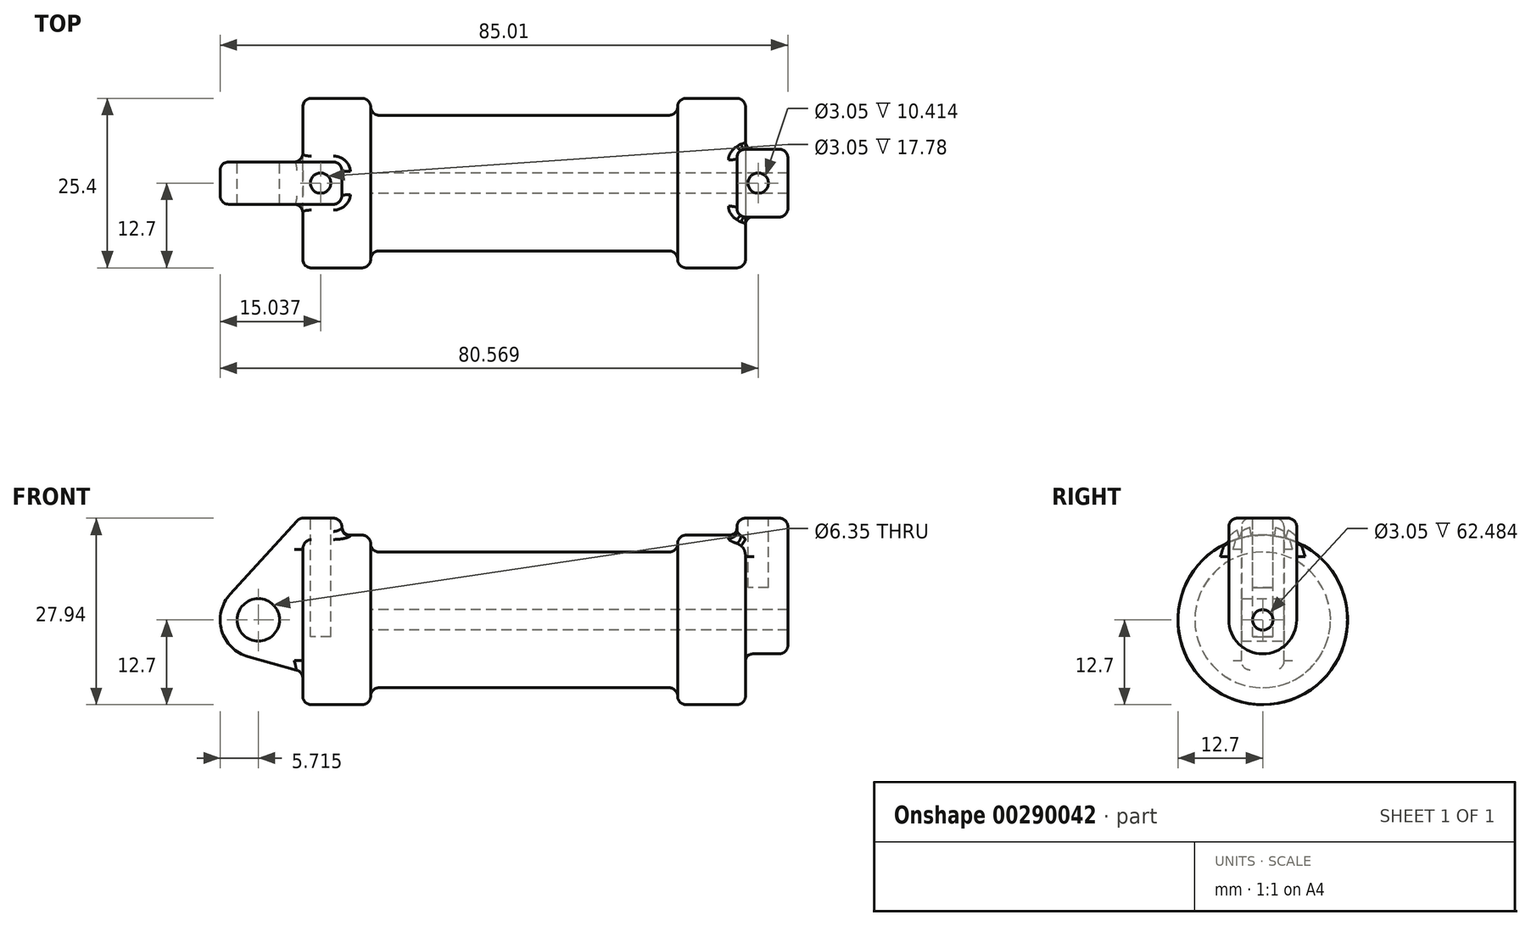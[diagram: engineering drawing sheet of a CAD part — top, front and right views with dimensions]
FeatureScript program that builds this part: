
annotation { "Feature Type Name" : "Feature", "Feature Type Description" : "" }
export const myFeature = defineFeature(function(context is Context, id is Id, definition is map)
    precondition{}
    {
        {
            var Q0;
            Q0=qCreatedBy(makeId("Front.planeOp"),FACE);
            var sketch = newSketch(context, id + "F0", { "sketchPlane" : qUnion([Q0])});
            skLineSegment(sketch, "E0", {"start": v(0, 0) * mm, "end": v(0, 12.7) * mm});
            skLineSegment(sketch, "E1", {"start": v(0, 12.7) * mm, "end": v(10.16, 12.7) * mm});
            skLineSegment(sketch, "E2", {"start": v(10.16, 12.7) * mm, "end": v(10.16, 10.16) * mm});
            skLineSegment(sketch, "E3", {"start": v(10.16, 10.16) * mm, "end": v(56.13, 10.16) * mm});
            skLineSegment(sketch, "E4", {"start": v(56.13, 10.16) * mm, "end": v(56.13, 12.7) * mm});
            skLineSegment(sketch, "E5", {"start": v(56.13, 12.7) * mm, "end": v(66.3, 12.7) * mm});
            skLineSegment(sketch, "E6", {"start": v(66.3, 12.7) * mm, "end": v(66.3, 0) * mm});
            skLineSegment(sketch, "E7", {"start": v(66.3, 0) * mm, "end": v(0, 0) * mm});
            skLineSegment(sketch, "E8", {"start": v(5.84, 15.24) * mm, "end": v(-0.5, 15.24) * mm});
            skLineSegment(sketch, "E9", {"start": v(-0.5, 15.24) * mm, "end": v(-10.88, 3.85) * mm});
            skLineSegment(sketch, "E10", {"start": v(0, 0) * mm, "end": v(-6.65, 0) * mm});
            skCircle(sketch, "E11", {"center": v(-6.65, 0) * mm, "radius": 5.72 * mm});
            skCircle(sketch, "E12", {"center": v(-6.65, 0) * mm, "radius": 3.18 * mm});
            skLineSegment(sketch, "E13", {"start": v(5.84, 15.24) * mm, "end": v(5.84, -9.4) * mm});
            skLineSegment(sketch, "E14", {"start": v(5.84, -9.4) * mm, "end": v(-8.18, -5.5) * mm});
            skSolve(sketch);
        }
        {
            var Q0;
            {var subQ0=sQuery(id+"F0.wireOp",EDGE,"E14");Q0=makeQuery(id+"F0.imprint","IMPRINT",FACE,{"disambiguationData":[TD([[makeQuery(id+"F0.imprint","IMPRINT",EDGE,{"derivedFrom":subQ0}),-1.0]])]});}
            var Q1;
            {var subQ5=sQuery(id+"F0.wireOp",EDGE,"E12");Q1=makeQuery(id+"F0.imprint","IMPRINT",FACE,{"disambiguationData":[TD([[makeQuery(id+"F0.imprint","IMPRINT",EDGE,{"derivedFrom":subQ5}),-1.0]])]});}
            var Q2;
            {var subQ1=sQuery(id+"F0.wireOp",EDGE,"E0");Q2=makeQuery(id+"F0.imprint","IMPRINT",FACE,{"disambiguationData":[TD([[makeQuery(id+"F0.imprint","IMPRINT",EDGE,{"derivedFrom":subQ1}),1.0]])]});}
            var Q3;
            {var subQ0=sQuery(id+"F0.wireOp",EDGE,"E0");Q3=makeQuery(id+"F0.imprint","IMPRINT",FACE,{"disambiguationData":[TD([[makeQuery(id+"F0.imprint","IMPRINT",EDGE,{"derivedFrom":subQ0}),-1.0]])]});}
            extrude(context, id + "F1", {"entities" : qUnion([Q0, Q1, Q2, Q3]), "endBound" : BoundingType.SYMMETRIC, "depth" : 6.35 * mm});
        }
        {
            var Q0;
            {var subQ0=sQuery(id+"F0.wireOp",EDGE,"E0");Q0=makeQuery(id+"F0.imprint","IMPRINT",FACE,{"disambiguationData":[TD([[makeQuery(id+"F0.imprint","IMPRINT",EDGE,{"derivedFrom":subQ0}),-1.0]])]});}
            var Q1;
            {var subQ0=sQuery(id+"F0.wireOp",EDGE,"E2");Q1=makeQuery(id+"F0.imprint","IMPRINT",FACE,{"disambiguationData":[TD([[makeQuery(id+"F0.imprint","IMPRINT",EDGE,{"derivedFrom":subQ0}),-1.0]])]});}
            var Q2;
            Q2=sQuery(id+"F0.wireOp",EDGE,"E7");
            revolve(context, id + "F2", {"operationType" : NewBodyOperationType.ADD, "entities" : qUnion([Q0, Q1]), "axis" : qUnion([Q2]), "revolveType" : RevolveType.FULL});
        }
        {
            var Q0;
            Q0=makeQuery(id+"F2.opRevolve","SWEPT_FACE",FACE,{"disambiguationData":[OSD([sQuery(id+"F0.wireOp",EDGE,"E6")])]});
            var sketch = newSketch(context, id + "F3", { "sketchPlane" : qUnion([Q0])});
            skCircle(sketch, "E15", {"center": v(0, 0) * mm, "radius": 5.08 * mm});
            skCircle(sketch, "E16", {"center": v(0, 0) * mm, "radius": 1.52 * mm});
            skLineSegment(sketch, "E17", {"start": v(-5.08, 0) * mm, "end": v(-5.08, 15.24) * mm});
            skLineSegment(sketch, "E18", {"start": v(-5.08, 15.24) * mm, "end": v(5.08, 15.24) * mm});
            skLineSegment(sketch, "E19", {"start": v(5.08, 15.24) * mm, "end": v(5.08, 0) * mm});
            skSolve(sketch);
        }
        {
            var Q0;
            Q0 = qSketchRegion(id + "F3", true);
            extrude(context, id + "F4", {"entities" : qUnion([Q0]), "operationType" : NewBodyOperationType.ADD, "depth" : 6.35 * mm, "hasSecondDirection" : true, "secondDirectionOppositeDirection" : true, "secondDirectionDepth" : 1.27 * mm});
        }
        {
            var Q0;
            Q0=makeQuery(id+"F3.imprint","IMPRINT",FACE,{"disambiguationData":[TD([[makeQuery(id+"F3.imprint","IMPRINT",EDGE,{"derivedFrom":sQuery(id+"F3.wireOp",EDGE,"E16")}),1.0]])]});
            var Q1;
            Q1=makeQuery(id+"F2.opRevolve","SWEPT_FACE",FACE,{"disambiguationData":[OSD([sQuery(id+"F0.wireOp",EDGE,"E2")])]});
            extrude(context, id + "F5", {"entities" : qUnion([Q0]), "operationType" : NewBodyOperationType.REMOVE, "endBound" : BoundingType.UP_TO_SURFACE, "oppositeDirection" : true, "endBoundEntityFace" : qUnion([Q1]), "depth" : 25.4 * mm});
        }
        {
            var Q0;
            {var subQ0=sQuery(id+"F3.wireOp",EDGE,"E18");Q0=makeQuery(id+"FFKBswe1jkoV0Kr_1.boolean.opBoolean","MERGE",FACE,{"derivedFrom":[makeQuery(id+"F4.opExtrude","SWEPT_FACE",FACE,{"disambiguationData":[OSD([subQ0])]}),makeQuery(id+"FFKBswe1jkoV0Kr_1.opExtrude","SWEPT_FACE",FACE,{"disambiguationData":[OSD([subQ0])]})]});}
            var sketch = newSketch(context, id + "F6", { "sketchPlane" : qUnion([Q0])});
            skCircle(sketch, "E20", {"center": v(68.2, 0) * mm, "radius": 1.52 * mm});
            skSolve(sketch);
        }
        {
            var Q0;
            Q0=makeQuery(id+"F6.imprint","IMPRINT",FACE,{"disambiguationData":[TD([[makeQuery(id+"F6.imprint","IMPRINT",EDGE,{"derivedFrom":sQuery(id+"F6.wireOp",EDGE,"E20")}),1.0]])]});
            extrude(context, id + "F7", {"entities" : qUnion([Q0]), "operationType" : NewBodyOperationType.REMOVE, "oppositeDirection" : true, "depth" : 10.4 * mm});
        }
        {
            var Q0;
            Q0=makeQuery(id+"F1.opExtrude","SWEPT_FACE",FACE,{"disambiguationData":[OSD([sQuery(id+"F0.wireOp",EDGE,"E8")])]});
            var sketch = newSketch(context, id + "F8", { "sketchPlane" : qUnion([Q0])});
            skCircle(sketch, "E21", {"center": v(2.67, 0) * mm, "radius": 1.52 * mm});
            skSolve(sketch);
        }
        {
            var Q0;
            Q0=makeQuery(id+"F8.imprint","IMPRINT",FACE,{"disambiguationData":[TD([[makeQuery(id+"F8.imprint","IMPRINT",EDGE,{"derivedFrom":sQuery(id+"F8.wireOp",EDGE,"E21")}),1.0]])]});
            extrude(context, id + "F9", {"entities" : qUnion([Q0]), "operationType" : NewBodyOperationType.REMOVE, "oppositeDirection" : true, "depth" : 17.78 * mm});
        }
        {
            var Q0;
            Q0=makeQuery(id+"F1.opExtrude","CAP_EDGE",EDGE,{"disambiguationData":[OSD([sQuery(id+"F0.wireOp",EDGE,"E9")])],"isStart":false});
            var Q1;
            Q1=makeQuery(id+"F1.opExtrude","CAP_EDGE",EDGE,{"disambiguationData":[OSD([sQuery(id+"F0.wireOp",EDGE,"E11")])],"isStart":false});
            var Q2;
            Q2=makeQuery(id+"F1.opExtrude","CAP_EDGE",EDGE,{"disambiguationData":[OSD([sQuery(id+"F0.wireOp",EDGE,"E11")])],"isStart":true});
            var Q3;
            Q3=makeQuery(id+"F1.opExtrude","CAP_EDGE",EDGE,{"disambiguationData":[OSD([sQuery(id+"F0.wireOp",EDGE,"E9")])],"isStart":true});
            var Q4;
            Q4=makeQuery(id+"F1.opExtrude","CAP_EDGE",EDGE,{"disambiguationData":[OSD([sQuery(id+"F0.wireOp",EDGE,"E14")])],"isStart":true});
            var Q5;
            Q5=makeQuery(id+"F1.opExtrude","CAP_EDGE",EDGE,{"disambiguationData":[OSD([sQuery(id+"F0.wireOp",EDGE,"E14")])],"isStart":false});
            var Q6;
            Q6=makeQuery(id+"F1.opExtrude","CAP_EDGE",EDGE,{"disambiguationData":[OSD([sQuery(id+"F0.wireOp",EDGE,"E8")])],"isStart":true});
            var Q7;
            Q7=makeQuery(id+"F1.opExtrude","SWEPT_EDGE",EDGE,{"disambiguationData":[OSD([sQuery(id+"F0.wireOp",EDGE,"E8"),sQuery(id+"F0.wireOp",EDGE,"E13")])]});
            var Q8;
            Q8=makeQuery(id+"F2.opRevolve","SWEPT_EDGE",EDGE,{"disambiguationData":[OSD([sQuery(id+"F0.wireOp",EDGE,"E0"),sQuery(id+"F0.wireOp",EDGE,"E1")])]});
            var Q9;
            Q9=makeQuery(id+"F2.opRevolve","SWEPT_EDGE",EDGE,{"disambiguationData":[OSD([sQuery(id+"F0.wireOp",EDGE,"E1"),sQuery(id+"F0.wireOp",EDGE,"E2")])]});
            var Q10;
            Q10=makeQuery(id+"F1.opExtrude","CAP_EDGE",EDGE,{"disambiguationData":[OSD([sQuery(id+"F0.wireOp",EDGE,"E8")])],"isStart":false});
            var Q11;
            Q11=makeQuery(id+"F1.opExtrude","SWEPT_EDGE",EDGE,{"disambiguationData":[OSD([sQuery(id+"F0.wireOp",EDGE,"E8"),sQuery(id+"F0.wireOp",EDGE,"E9")])]});
            var Q12;
            Q12=makeQuery(id+"F2.boolean.opBoolean","INTERSECT",EDGE,{"derivedFrom":[makeQuery(id+"F1.opExtrude","CAP_FACE",FACE,{"disambiguationData":[OSD([sQuery(id+"F0.wireOp",EDGE,"E8"),sQuery(id+"F0.wireOp",EDGE,"E9"),sQuery(id+"F0.wireOp",EDGE,"E11"),sQuery(id+"F0.wireOp",EDGE,"E12"),sQuery(id+"F0.wireOp",EDGE,"E13"),sQuery(id+"F0.wireOp",EDGE,"E14")])],"isStart":false}),makeQuery(id+"F2.opRevolve","SWEPT_FACE",FACE,{"disambiguationData":[OSD([sQuery(id+"F0.wireOp",EDGE,"E1")])]})]});
            var Q13;
            Q13=makeQuery(id+"F2.boolean.opBoolean","INTERSECT",EDGE,{"derivedFrom":[makeQuery(id+"F1.opExtrude","SWEPT_FACE",FACE,{"disambiguationData":[OSD([sQuery(id+"F0.wireOp",EDGE,"E13")])]}),makeQuery(id+"F2.opRevolve","SWEPT_FACE",FACE,{"disambiguationData":[OSD([sQuery(id+"F0.wireOp",EDGE,"E1")])]})]});
            var Q14;
            Q14=makeQuery(id+"F2.boolean.opBoolean","INTERSECT",EDGE,{"derivedFrom":[makeQuery(id+"F1.opExtrude","CAP_FACE",FACE,{"disambiguationData":[OSD([sQuery(id+"F0.wireOp",EDGE,"E8"),sQuery(id+"F0.wireOp",EDGE,"E9"),sQuery(id+"F0.wireOp",EDGE,"E11"),sQuery(id+"F0.wireOp",EDGE,"E12"),sQuery(id+"F0.wireOp",EDGE,"E13"),sQuery(id+"F0.wireOp",EDGE,"E14")])],"isStart":true}),makeQuery(id+"F2.opRevolve","SWEPT_FACE",FACE,{"disambiguationData":[OSD([sQuery(id+"F0.wireOp",EDGE,"E1")])]})]});
            var Q15;
            Q15=makeQuery(id+"F2.opRevolve","SWEPT_EDGE",EDGE,{"disambiguationData":[OSD([sQuery(id+"F0.wireOp",EDGE,"E2"),sQuery(id+"F0.wireOp",EDGE,"E3")])]});
            var Q16;
            Q16=makeQuery(id+"F2.boolean.opBoolean","INTERSECT",EDGE,{"derivedFrom":[makeQuery(id+"F1.opExtrude","CAP_FACE",FACE,{"disambiguationData":[OSD([sQuery(id+"F0.wireOp",EDGE,"E8"),sQuery(id+"F0.wireOp",EDGE,"E9"),sQuery(id+"F0.wireOp",EDGE,"E11"),sQuery(id+"F0.wireOp",EDGE,"E12"),sQuery(id+"F0.wireOp",EDGE,"E13"),sQuery(id+"F0.wireOp",EDGE,"E14")])],"isStart":true}),makeQuery(id+"F2.opRevolve","SWEPT_FACE",FACE,{"disambiguationData":[OSD([sQuery(id+"F0.wireOp",EDGE,"E0")])]})]});
            var Q17;
            Q17=makeQuery(id+"F2.boolean.opBoolean","INTERSECT",EDGE,{"derivedFrom":[makeQuery(id+"F1.opExtrude","CAP_FACE",FACE,{"disambiguationData":[OSD([sQuery(id+"F0.wireOp",EDGE,"E8"),sQuery(id+"F0.wireOp",EDGE,"E9"),sQuery(id+"F0.wireOp",EDGE,"E11"),sQuery(id+"F0.wireOp",EDGE,"E12"),sQuery(id+"F0.wireOp",EDGE,"E13"),sQuery(id+"F0.wireOp",EDGE,"E14")])],"isStart":false}),makeQuery(id+"F2.opRevolve","SWEPT_FACE",FACE,{"disambiguationData":[OSD([sQuery(id+"F0.wireOp",EDGE,"E0")])]})]});
            var Q18;
            Q18=makeQuery(id+"F1.opExtrude","CAP_EDGE",EDGE,{"disambiguationData":[OSD([sQuery(id+"F0.wireOp",EDGE,"E13")])],"isStart":true});
            var Q19;
            Q19=makeQuery(id+"F1.opExtrude","CAP_EDGE",EDGE,{"disambiguationData":[OSD([sQuery(id+"F0.wireOp",EDGE,"E13")])],"isStart":false});
            var Q20;
            Q20=makeQuery(id+"F2.boolean.opBoolean","INTERSECT",EDGE,{"derivedFrom":[makeQuery(id+"F1.opExtrude","SWEPT_FACE",FACE,{"disambiguationData":[OSD([sQuery(id+"F0.wireOp",EDGE,"E14")])]}),makeQuery(id+"F2.opRevolve","SWEPT_FACE",FACE,{"disambiguationData":[OSD([sQuery(id+"F0.wireOp",EDGE,"E0")])]})]});
            fillet(context, id + "F10", {"entities" : qUnion([Q0, Q1, Q2, Q3, Q4, Q5, Q6, Q7, Q8, Q9, Q10, Q11, Q12, Q13, Q14, Q15, Q16, Q17, Q18, Q19, Q20]), "radius" : 1.27 * mm, "tangentPropagation" : true, "allowEdgeOverflow" : false});
        }
        {
            var Q0;
            Q0=makeQuery(id+"F2.opRevolve","SWEPT_EDGE",EDGE,{"disambiguationData":[OSD([sQuery(id+"F0.wireOp",EDGE,"E4"),sQuery(id+"F0.wireOp",EDGE,"E5")])]});
            var Q1;
            Q1=makeQuery(id+"F2.opRevolve","SWEPT_FACE",FACE,{"disambiguationData":[OSD([sQuery(id+"F0.wireOp",EDGE,"E3")])]});
            var Q2;
            Q2=makeQuery(id+"F4.opExtrude","CAP_EDGE",EDGE,{"disambiguationData":[OSD([sQuery(id+"F3.wireOp",EDGE,"E19")])],"isStart":true});
            var Q3;
            Q3=makeQuery(id+"F4.opExtrude","CAP_EDGE",EDGE,{"disambiguationData":[OSD([sQuery(id+"F3.wireOp",EDGE,"E17")])],"isStart":true});
            fillet(context, id + "F11", {"entities" : qUnion([Q0, Q1, Q2, Q3]), "radius" : 1.27 * mm, "tangentPropagation" : true, "allowEdgeOverflow" : false});
        }
        {
            var Q0;
            Q0=makeQuery(id+"F4.opExtrude","SWEPT_EDGE",EDGE,{"disambiguationData":[OSD([sQuery(id+"F3.wireOp",EDGE,"E17"),sQuery(id+"F3.wireOp",EDGE,"E18")])]});
            var Q1;
            Q1=makeQuery(id+"F4.opExtrude","CAP_EDGE",EDGE,{"disambiguationData":[OSD([sQuery(id+"F3.wireOp",EDGE,"E18")])],"isStart":true});
            var Q2;
            Q2=makeQuery(id+"F4.opExtrude","CAP_EDGE",EDGE,{"disambiguationData":[OSD([sQuery(id+"F3.wireOp",EDGE,"E18")])],"isStart":false});
            var Q3;
            Q3=makeQuery(id+"F4.opExtrude","SWEPT_EDGE",EDGE,{"disambiguationData":[OSD([sQuery(id+"F3.wireOp",EDGE,"E18"),sQuery(id+"F3.wireOp",EDGE,"E19")])]});
            var Q4;
            Q4=makeQuery(id+"F4.opExtrude","CAP_EDGE",EDGE,{"disambiguationData":[OSD([sQuery(id+"F3.wireOp",EDGE,"E17")])],"isStart":false});
            var Q5;
            Q5=makeQuery(id+"F2.opRevolve","SWEPT_EDGE",EDGE,{"disambiguationData":[OSD([sQuery(id+"F0.wireOp",EDGE,"E5"),sQuery(id+"F0.wireOp",EDGE,"E6")])]});
            fillet(context, id + "F12", {"entities" : qUnion([Q0, Q1, Q2, Q3, Q4, Q5]), "radius" : 1.27 * mm, "tangentPropagation" : true, "allowEdgeOverflow" : false});
        }
        {
            var Q0;
            Q0=makeQuery(id+"F4.opExtrude","SWEPT_FACE",FACE,{"disambiguationData":[OSD([sQuery(id+"F3.wireOp",EDGE,"E17")])]});
            fillet(context, id + "F13", {"entities" : qUnion([Q0]), "radius" : 1.27 * mm, "tangentPropagation" : true, "rho" : 0.5, "crossSection" : FilletCrossSection.CONIC, "allowEdgeOverflow" : false});
        }
    });
